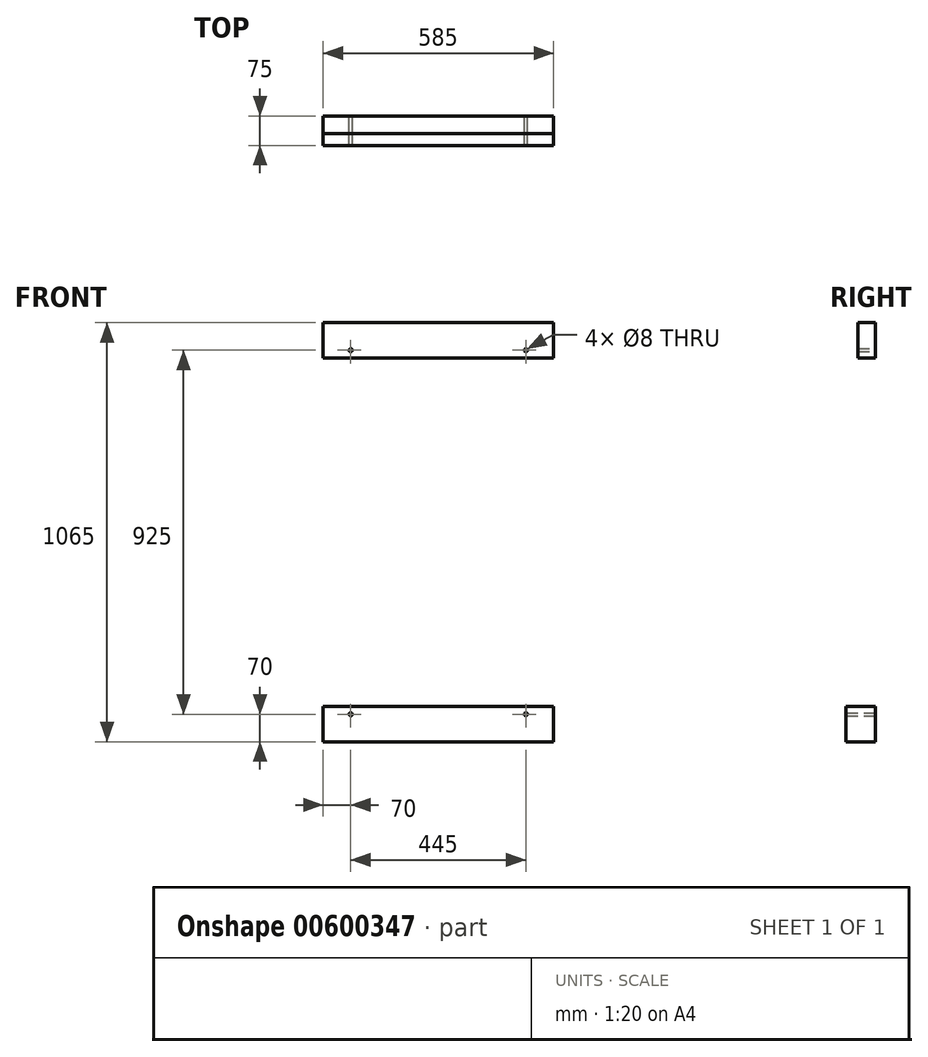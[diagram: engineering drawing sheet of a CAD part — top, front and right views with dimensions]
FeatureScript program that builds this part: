
annotation { "Feature Type Name" : "Feature", "Feature Type Description" : "" }
export const myFeature = defineFeature(function(context is Context, id is Id, definition is map)
    precondition{}
    {
        {
            var Q0;
            Q0=qCreatedBy(makeId("Front.planeOp"),FACE);
            var sketch = newSketch(context, id + "F0", { "sketchPlane" : qUnion([Q0])});
            skLineSegment(sketch, "E0.bottom", {"start": v(0, 0) * mm, "end": v(585, 0) * mm});
            skLineSegment(sketch, "E0.top", {"start": v(0, 90) * mm, "end": v(585, 90) * mm});
            skLineSegment(sketch, "E0.left", {"start": v(0, 0) * mm, "end": v(0, 90) * mm});
            skLineSegment(sketch, "E0.right", {"start": v(585, 0) * mm, "end": v(585, 90) * mm});
            skLineSegment(sketch, "E1.bottom", {"start": v(0, 0) * mm, "end": v(90, 0) * mm});
            skLineSegment(sketch, "E1.top", {"start": v(0, -885) * mm, "end": v(90, -885) * mm});
            skLineSegment(sketch, "E1.left", {"start": v(0, 0) * mm, "end": v(0, -885) * mm});
            skLineSegment(sketch, "E1.right", {"start": v(90, 0) * mm, "end": v(90, -885) * mm});
            skLineSegment(sketch, "E2.bottom", {"start": v(0, -885) * mm, "end": v(585, -885) * mm});
            skLineSegment(sketch, "E2.top", {"start": v(0, -975) * mm, "end": v(585, -975) * mm});
            skLineSegment(sketch, "E2.left", {"start": v(0, -885) * mm, "end": v(0, -975) * mm});
            skLineSegment(sketch, "E2.right", {"start": v(585, -885) * mm, "end": v(585, -975) * mm});
            skLineSegment(sketch, "E3.bottom", {"start": v(585, -885) * mm, "end": v(495, -885) * mm});
            skLineSegment(sketch, "E3.top", {"start": v(585, 0) * mm, "end": v(495, 0) * mm});
            skLineSegment(sketch, "E3.left", {"start": v(585, -885) * mm, "end": v(585, 0) * mm});
            skLineSegment(sketch, "E3.right", {"start": v(495, -885) * mm, "end": v(495, 0) * mm});
            skLineSegment(sketch, "E4.0", {"start": v(0, 30) * mm, "end": v(585, 30) * mm, "construction": true});
            skLineSegment(sketch, "E5.0", {"start": v(525, -885) * mm, "end": v(525, 0) * mm, "construction": true});
            skLineSegment(sketch, "E6.0", {"start": v(0, -915) * mm, "end": v(585, -915) * mm, "construction": true});
            skLineSegment(sketch, "E7.0", {"start": v(60, 0) * mm, "end": v(60, -885) * mm, "construction": true});
            skLineSegment(sketch, "E8", {"start": v(525, 0) * mm, "end": v(525, 30) * mm, "construction": true});
            skLineSegment(sketch, "E9", {"start": v(60, 0) * mm, "end": v(60, 30) * mm, "construction": true});
            skLineSegment(sketch, "E10", {"start": v(525, -885) * mm, "end": v(525, -915) * mm, "construction": true});
            skLineSegment(sketch, "E11", {"start": v(60, -885) * mm, "end": v(60, -915) * mm, "construction": true});
            skLineSegment(sketch, "E12.0", {"start": v(515, 0) * mm, "end": v(515, 30) * mm, "construction": true});
            skLineSegment(sketch, "E13.0", {"start": v(0, 20) * mm, "end": v(585, 20) * mm, "construction": true});
            skCircle(sketch, "E14", {"center": v(515, 20) * mm, "radius": 4 * mm});
            skLineSegment(sketch, "E15.0", {"start": v(70, 0) * mm, "end": v(70, 30) * mm, "construction": true});
            skCircle(sketch, "E16", {"center": v(70, 20) * mm, "radius": 4 * mm});
            skLineSegment(sketch, "E17.0", {"start": v(515, -885) * mm, "end": v(515, -915) * mm, "construction": true});
            skLineSegment(sketch, "E18.0", {"start": v(0, -905) * mm, "end": v(585, -905) * mm, "construction": true});
            skLineSegment(sketch, "E19.0", {"start": v(70, -885) * mm, "end": v(70, -915) * mm, "construction": true});
            skCircle(sketch, "E20", {"center": v(70, -905) * mm, "radius": 4 * mm});
            skCircle(sketch, "E21", {"center": v(515, -905) * mm, "radius": 4 * mm});
            skSolve(sketch);
        }
        {
            var Q0;
            Q0=makeQuery(id+"F0.imprint","IMPRINT",FACE,{"disambiguationData":[TD([[makeQuery(id+"F0.imprint","IMPRINT",EDGE,{"derivedFrom":sQuery(id+"F0.wireOp",EDGE,"E3.bottom")}),-1.0]])]});
            var Q1;
            Q1=makeQuery(id+"F0.imprint","IMPRINT",FACE,{"disambiguationData":[TD([[makeQuery(id+"F0.imprint","IMPRINT",EDGE,{"derivedFrom":sQuery(id+"F0.wireOp",EDGE,"E2.top")}),1.0]])]});
            var Q2;
            Q2=makeQuery(id+"F0.imprint","IMPRINT",FACE,{"disambiguationData":[TD([[makeQuery(id+"F0.imprint","IMPRINT",EDGE,{"derivedFrom":sQuery(id+"F0.wireOp",EDGE,"E1.bottom")}),-1.0]])]});
            var Q3;
            Q3=makeQuery(id+"F0.imprint","IMPRINT",FACE,{"disambiguationData":[TD([[makeQuery(id+"F0.imprint","IMPRINT",EDGE,{"derivedFrom":sQuery(id+"F0.wireOp",EDGE,"E0.bottom")}),1.0]])]});
            extrude(context, id + "F1", {"entities" : qUnion([Q0, Q1, Q2, Q3]), "depth" : 45 * mm, "offsetDistance" : 25 * mm});
        }
        {
            var Q0;
            Q0=makeQuery(id+"F0.imprint","IMPRINT",FACE,{"disambiguationData":[TD([[makeQuery(id+"F0.imprint","IMPRINT",EDGE,{"derivedFrom":sQuery(id+"F0.wireOp",EDGE,"E2.top")}),1.0]])]});
            var Q1;
            Q1=makeQuery(id+"F0.imprint","IMPRINT",FACE,{"disambiguationData":[TD([[makeQuery(id+"F0.imprint","IMPRINT",EDGE,{"derivedFrom":sQuery(id+"F0.wireOp",EDGE,"E1.bottom")}),-1.0]])]});
            var Q2;
            Q2=makeQuery(id+"F0.imprint","IMPRINT",FACE,{"disambiguationData":[TD([[makeQuery(id+"F0.imprint","IMPRINT",EDGE,{"derivedFrom":sQuery(id+"F0.wireOp",EDGE,"E3.bottom")}),-1.0]])]});
            extrude(context, id + "F2", {"entities" : qUnion([Q0, Q1, Q2]), "operationType" : NewBodyOperationType.ADD, "depth" : 75 * mm, "offsetDistance" : 25 * mm});
        }
        {
            var Q0;
            Q0=qCreatedBy(makeId("Top.planeOp"),FACE);
            var sketch = newSketch(context, id + "F3", { "sketchPlane" : qUnion([Q0])});
            skLineSegment(sketch, "E22", {"start": v(0, 0) * mm, "end": v(0, -75) * mm});
            skLineSegment(sketch, "E23.bottom", {"start": v(0, 0) * mm, "end": v(90, 0) * mm});
            skLineSegment(sketch, "E23.top", {"start": v(0, -75) * mm, "end": v(90, -75) * mm});
            skLineSegment(sketch, "E23.right", {"start": v(90, 0) * mm, "end": v(90, -75) * mm});
            skLineSegment(sketch, "E24.bottom", {"start": v(90, -75) * mm, "end": v(0, -75) * mm});
            skLineSegment(sketch, "E24.top", {"start": v(90, -45) * mm, "end": v(0, -45) * mm});
            skLineSegment(sketch, "E24.left", {"start": v(90, -75) * mm, "end": v(90, -45) * mm});
            skLineSegment(sketch, "E24.right", {"start": v(0, -75) * mm, "end": v(0, -45) * mm});
            skLineSegment(sketch, "E25.0", {"start": v(90, -60) * mm, "end": v(0, -60) * mm, "construction": true});
            skLineSegment(sketch, "E26.bottom", {"start": v(80, -63) * mm, "end": v(90, -63) * mm});
            skLineSegment(sketch, "E26.top", {"start": v(80, -57) * mm, "end": v(90, -57) * mm});
            skLineSegment(sketch, "E26.left", {"start": v(80, -63) * mm, "end": v(80, -57) * mm});
            skPoint(sketch, "E26.middle", {"position": v(90, -60) * mm});
            skLineSegment(sketch, "E27", {"start": v(90, -63) * mm, "end": v(90, -57) * mm});
            skSolve(sketch);
        }
        {
            var Q0;
            Q0=makeQuery(id+"F3.imprint","IMPRINT",FACE,{"disambiguationData":[TD([[makeQuery(id+"F3.imprint","IMPRINT",EDGE,{"derivedFrom":sQuery(id+"F3.wireOp",EDGE,"E26.bottom")}),1.0]])]});
            var Q1;
            {var subQ0=sQuery(id+"F0.wireOp",EDGE,"E2.bottom");Q1=makeQuery(id+"F2.boolean.opBoolean","MERGE",FACE,{"derivedFrom":[makeQuery(id+"F1.opExtrude","SWEPT_FACE",FACE,{"disambiguationData":[OSD([subQ0])]}),makeQuery(id+"F2.opExtrude","SWEPT_FACE",FACE,{"disambiguationData":[OSD([subQ0])]})]});}
            extrude(context, id + "F4", {"entities" : qUnion([Q0]), "operationType" : NewBodyOperationType.REMOVE, "endBound" : BoundingType.UP_TO_SURFACE, "oppositeDirection" : true, "depth" : 25 * mm, "endBoundEntityFace" : qUnion([Q1]), "offsetDistance" : 25 * mm});
        }
    });
